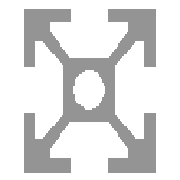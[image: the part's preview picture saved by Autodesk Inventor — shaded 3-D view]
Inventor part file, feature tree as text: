
AUTODESK INVENTOR PART (.ipt)
format: ipt  version: 2024 (Build 280153000, 153)  size: 233,984 bytes
history: native  units: in
note: dims shown in document units (in); Inventor stores cm internally (conversion verified against a paired STEP export)
features: other x37, extrude x1, fillet x1
ambient origin geometry x8: Origin, YZ Plane, XZ Plane, XY Plane, X Axis, Y Axis, Z Axis, Center Point
bodies: Body1 (feature_tree)
feature tree (39):
  other  "Table"
  other  "20x20 Channel-10"
  other  "20x20 Channel-20"
  other  "20x20 Channel-30"
  other  "20x20 Channel-40"
  other  "20x20 Channel-50"
  other  "20x20 Channel-100"
  other  "20x20 Channel-150"
  other  "20x20 Channel-200"
  other  "20x20 Channel-250"
  other  "20x20 Channel-300"
  other  "20x20 Channel-350"
  other  "20x20 Channel-400"
  other  "20x20 Channel-450"
  other  "20x20 Channel-500"
  other  "20x20 Channel-550"
  other  "20x20 Channel-560"
  other  "20x20 Channel-570"
  other  "20x20 Channel-580"
  other  "20x20 Channel-590"
  other  "20x20 Channel-600"
  other  "20x20 Channel-610"
  other  "20x20 Channel-620"
  other  "20x20 Channel-630"
  other  "20x20 Channel-640"
  other  "20x20 Channel-650"
  other  "CH-1-01-20x20 Channel-427"
  other  "CH-1-01-20x20 Channel-428"
  other  "CH-1-01-20x20 Channel-372"
  other  "CH-1-01-20x20 Channel-437"
  other  "CH-1-01-20x20 Channel-604"
  other  "CH-1-01-20x20 Channel-528"
  other  "CH-1-01-20x20 Channel-900"
  other  "CH-1-01-20x20 Channel-540"
  other  "CH-1-01-20x20 Channel-860"
  other  "CH-1-01-20x20 Channel-270"
  other  "CH-1-01-20x20 Channel-37.5"
  extrude  "Extrusion3"  Depth=0.7874in
  fillet  "Fillet2"  Radius=0.7874in
